# Revit family: Haworth_Compose_Panel_StackSolid
name_source: partatom
category: Furniture Systems
revit_build: Autodesk Revit 2018 (Build: 20170223_1515(x64)
units: mm (PartAtom-declared; Revit-internal decimal feet)

## family parameters
Always vertical = Yes
Cut with Voids When Loaded = No
OmniClass Number = 23.40.70.14.64.21
OmniClass Title = Systems Furniture
Part Type = Normal
Room Calculation Point = No
Round Connector Dimension = Use Diameter
Shared = No
Work Plane-Based = No

## types (9) — shared parameters
Actual Height = 15 7/8"
Assembly Code = E2020500
Back Panel Finish = Haworth _ Fabric _ Striae _ Moonlight C1-AC
Description = Haworth - Compose Panel Solid - Stack
Frame Depth = 2 3/4"
Frame Width = 3/4"
Front Panel Finish = Haworth _ Fabric _ Striae _ Moonlight C1-AC
Manufacturer = Haworth
Max. Height = 24"
Max. Width = 96"
Min. Height = 16"
Min. Width = 18"
Min/Max Width = 18-60 in. @ 6 in. Increments
Model = VZFS
Panel Depth = 1/2"
Panel Height = 15 1/2"
Revision Number = 5
Size = Verify Final Dim. w/ Haworth
Sustainability Info = http://media.haworth.com
Top Trim = Yes
Top Trim Adjuster = 1/8"
Top Trim Width = 1/8"
Trim Depth = 3"
Trim Finish = Haworth _ Metal _ Brushed Aluminum
Trim Thin Profile = Yes
URL = www.haworth.com
URL - Product = http://www.haworth.com
Vertical Trim Width = 1/4"
Warranty = http://www.haworth.com

## per-type parameters (varying)
| type | Actual Width | Custom Size | Panel Width | Width |
| 18w | 18" | No | 18" | 18" |
| 24w | 24" | No | 24" | 24" |
| 30w | 30" | No | 30" | 30" |
| 36w | 36" | No | 36" | 36" |
| 42w | 42" | No | 42" | 42" |
| 48w | 48" | No | 48" | 48" |
| 54w | 54" | No | 54" | 54" |
| 60w | 60" | No | 60" | 60" |
| 66w | 66" | Yes | 66" | 66" |

## geometry (parser evidence)
native form markers: Sweep x10
no freeform markers — native parametric forms only
